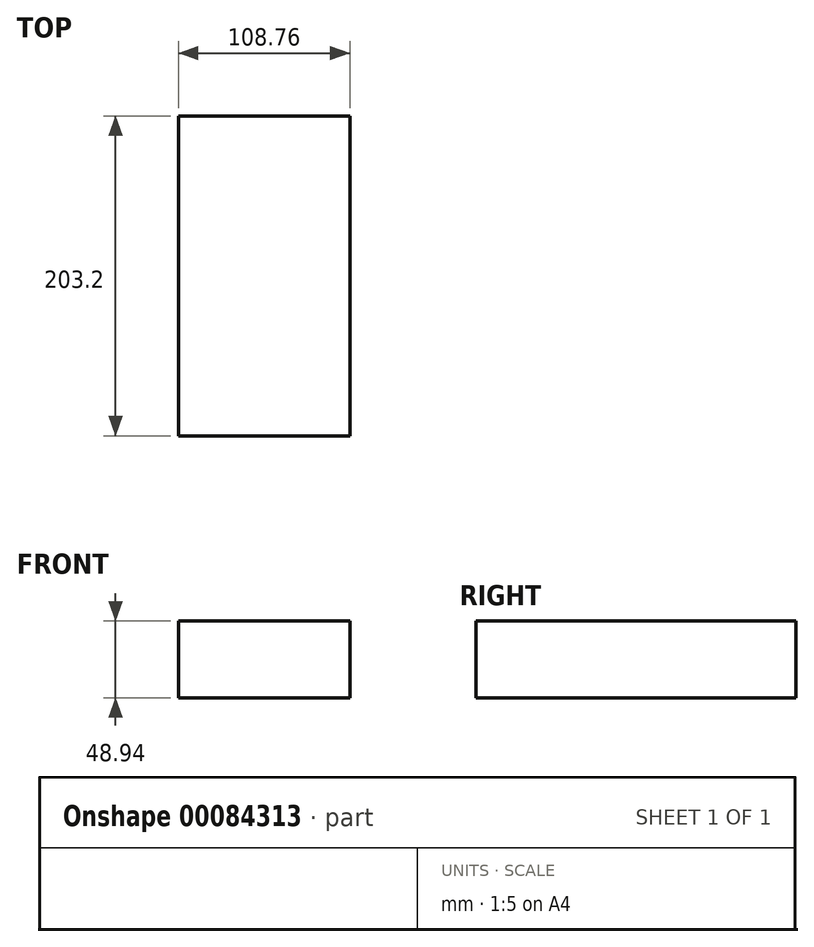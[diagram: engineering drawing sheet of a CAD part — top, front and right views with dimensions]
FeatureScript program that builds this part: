
annotation { "Feature Type Name" : "Feature", "Feature Type Description" : "" }
export const myFeature = defineFeature(function(context is Context, id is Id, definition is map)
    precondition{}
    {
        {
            var Q0;
            Q0=qCreatedBy(makeId("Front.planeOp"),FACE);
            var sketch = newSketch(context, id + "F0", { "sketchPlane" : qUnion([Q0])});
            skLineSegment(sketch, "E0.bottom", {"start": v(-54.38, 20.62) * mm, "end": v(54.38, 20.62) * mm});
            skLineSegment(sketch, "E0.top", {"start": v(-54.38, -28.32) * mm, "end": v(54.38, -28.32) * mm});
            skLineSegment(sketch, "E0.left", {"start": v(-54.38, 20.62) * mm, "end": v(-54.38, -28.32) * mm});
            skLineSegment(sketch, "E0.right", {"start": v(54.38, 20.62) * mm, "end": v(54.38, -28.32) * mm});
            skPoint(sketch, "E0.middle", {"position": v(0, -3.85) * mm});
            skSolve(sketch);
        }
        {
            var Q0;
            Q0 = qSketchRegion(id + "F0", true);
            extrude(context, id + "F1", {"entities" : qUnion([Q0]), "depth" : 203.2 * mm});
        }
    });
